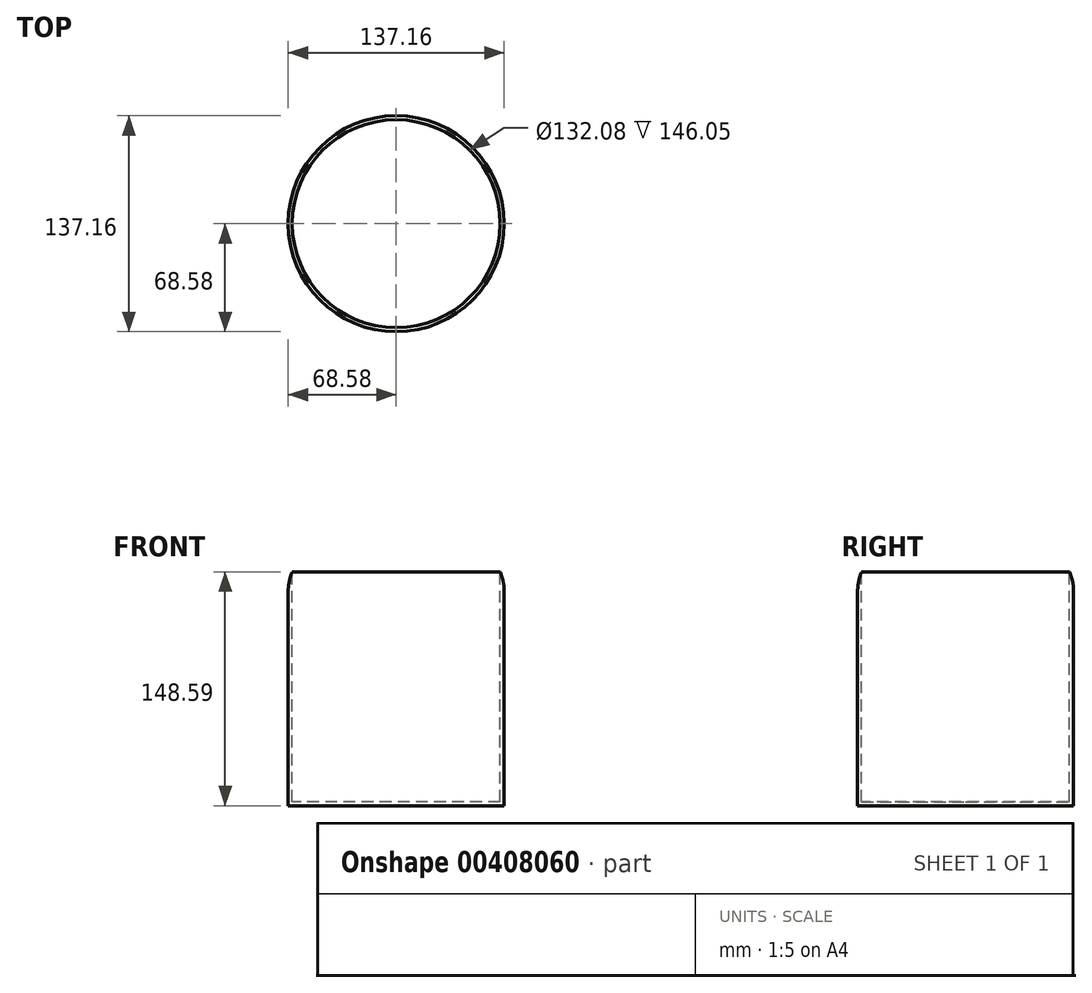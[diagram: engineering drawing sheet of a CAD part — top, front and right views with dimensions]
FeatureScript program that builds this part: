
annotation { "Feature Type Name" : "Feature", "Feature Type Description" : "" }
export const myFeature = defineFeature(function(context is Context, id is Id, definition is map)
    precondition{}
    {
        {
            var Q0;
            Q0=qCreatedBy(makeId("Top.planeOp"),FACE);
            var sketch = newSketch(context, id + "F0", { "sketchPlane" : qUnion([Q0])});
            skCircle(sketch, "E0", {"center": v(0, 0) * mm, "radius": 68.58 * mm});
            skSolve(sketch);
        }
        {
            var Q0;
            Q0 = qSketchRegion(id + "F0", true);
            extrude(context, id + "F1", {"entities" : qUnion([Q0]), "oppositeDirection" : true, "depth" : 148.6 * mm});
        }
        {
            var Q0;
            Q0=makeQuery(id+"F1.opExtrude","CAP_FACE",FACE,{"disambiguationData":[OSD([sQuery(id+"F0.wireOp",EDGE,"E0")])],"isStart":true});
            shell(context, id + "F2", {"entities" : qUnion([Q0]), "thickness" : 2.54 * mm});
        }
        {
            var Q0;
            Q0=makeQuery(id+"F1.opExtrude","CAP_EDGE",EDGE,{"disambiguationData":[OSD([sQuery(id+"F0.wireOp",EDGE,"E0")])],"isStart":true});
            fillet(context, id + "F3", {"entities" : qUnion([Q0]), "radius" : 31.27 * mm, "tangentPropagation" : true, "allowEdgeOverflow" : false});
        }
    });
